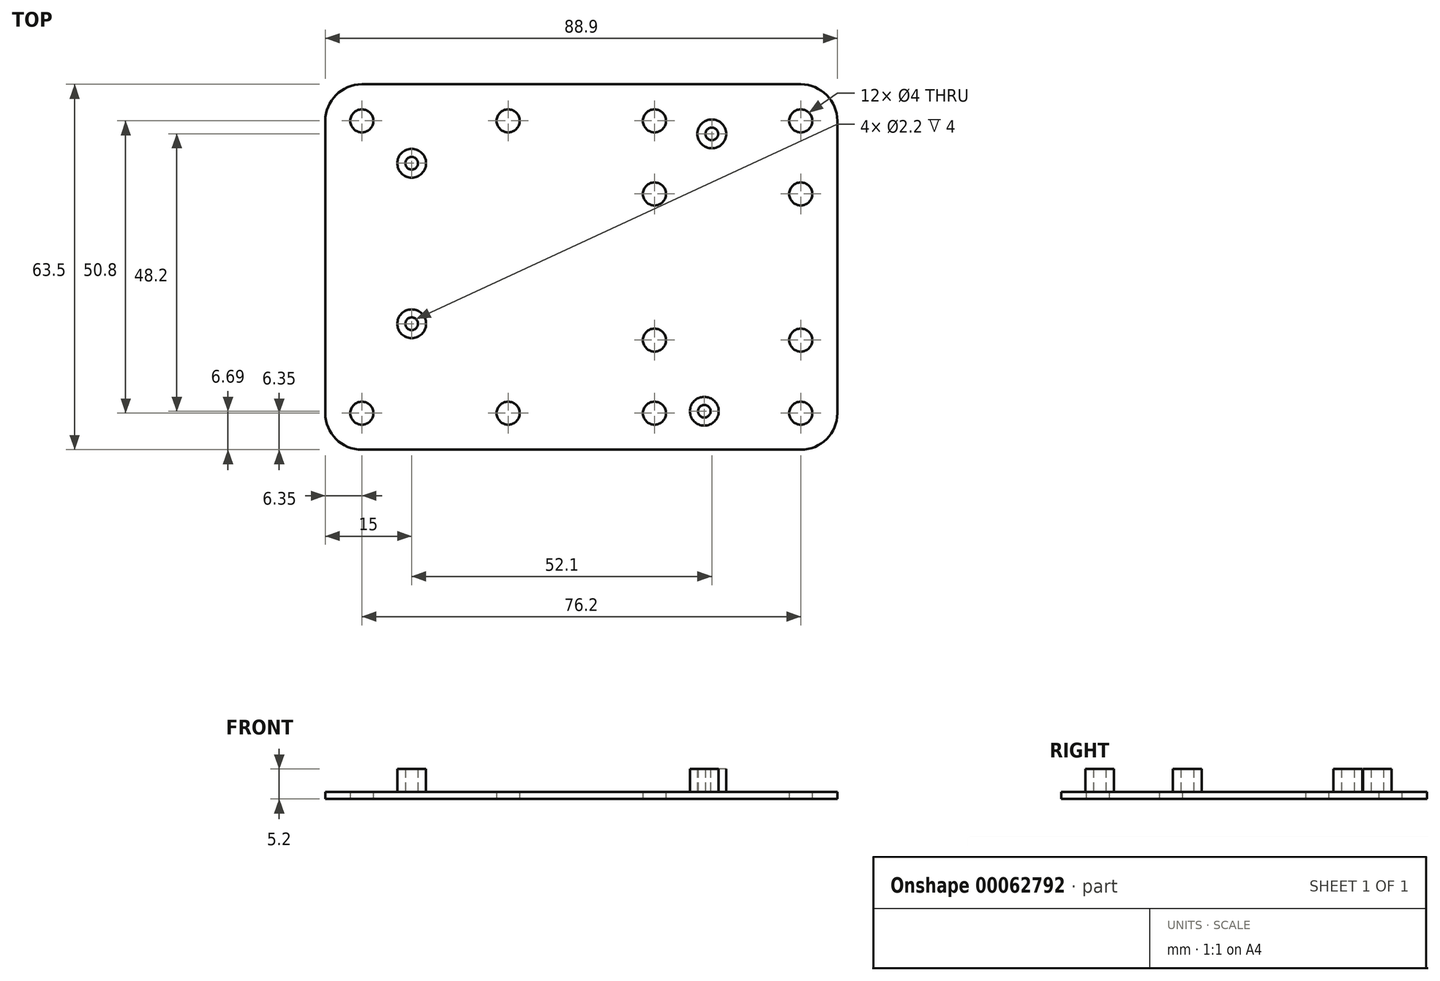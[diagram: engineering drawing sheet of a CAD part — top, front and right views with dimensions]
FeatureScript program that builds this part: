
annotation { "Feature Type Name" : "Feature", "Feature Type Description" : "" }
export const myFeature = defineFeature(function(context is Context, id is Id, definition is map)
    precondition{}
    {
        {
            var Q0;
            Q0=qCreatedBy(makeId("Top.planeOp"),FACE);
            var sketch = newSketch(context, id + "F0", { "sketchPlane" : qUnion([Q0])});
            skLineSegment(sketch, "E0.bottom", {"start": v(38.1, -31.75) * mm, "end": v(-38.1, -31.75) * mm});
            skLineSegment(sketch, "E0.top", {"start": v(38.1, 31.75) * mm, "end": v(-38.1, 31.75) * mm});
            skLineSegment(sketch, "E0.left", {"start": v(44.45, -25.4) * mm, "end": v(44.45, 25.4) * mm});
            skLineSegment(sketch, "E0.right", {"start": v(-44.45, -25.4) * mm, "end": v(-44.45, 25.4) * mm});
            skPoint(sketch, "E0.middle", {"position": v(0, 0) * mm});
            skPoint(sketch, "E1.visualSharp", {"position": v(-44.45, 31.75) * mm});
            skArc(sketch, "E1.filletArc", {"start": v(-38.1, 31.75) * mm, "mid": v(-42.6, 29.9) * mm, "end": v(-44.45, 25.4) * mm});
            skPoint(sketch, "E2.visualSharp", {"position": v(44.45, 31.75) * mm});
            skArc(sketch, "E2.filletArc", {"start": v(44.45, 25.4) * mm, "mid": v(42.6, 29.9) * mm, "end": v(38.1, 31.75) * mm});
            skPoint(sketch, "E3.visualSharp", {"position": v(44.45, -31.75) * mm});
            skArc(sketch, "E3.filletArc", {"start": v(38.1, -31.75) * mm, "mid": v(42.6, -29.9) * mm, "end": v(44.45, -25.4) * mm});
            skPoint(sketch, "E4.visualSharp", {"position": v(-44.45, -31.75) * mm});
            skArc(sketch, "E4.filletArc", {"start": v(-44.45, -25.4) * mm, "mid": v(-42.6, -29.9) * mm, "end": v(-38.1, -31.75) * mm});
            skCircle(sketch, "E5", {"center": v(-38.1, -25.4) * mm, "radius": 2 * mm});
            skCircle(sketch, "E6.0.1.0", {"center": v(-38.1, 25.4) * mm, "radius": 2 * mm});
            skCircle(sketch, "E6.1.0.0", {"center": v(-12.7, -25.4) * mm, "radius": 2 * mm});
            skCircle(sketch, "E6.1.1.0", {"center": v(-12.7, 25.4) * mm, "radius": 2 * mm});
            skCircle(sketch, "E6.2.0.0", {"center": v(12.7, -25.4) * mm, "radius": 2 * mm});
            skCircle(sketch, "E6.2.1.0", {"center": v(12.7, 25.4) * mm, "radius": 2 * mm});
            skLineSegment(sketch, "E6.direction1", {"start": v(-38.1, -25.4) * mm, "end": v(-12.7, -25.4) * mm, "construction": true});
            skLineSegment(sketch, "E6.direction2", {"start": v(-38.1, -25.4) * mm, "end": v(-38.1, 25.4) * mm, "construction": true});
            skCircle(sketch, "E7.0.3.0", {"center": v(38.1, -25.4) * mm, "radius": 2 * mm});
            skCircle(sketch, "E7.0.3.1", {"center": v(38.1, 25.4) * mm, "radius": 2 * mm});
            skCircle(sketch, "E8.0.1.0", {"center": v(38.1, -12.7) * mm, "radius": 2 * mm});
            skLineSegment(sketch, "E8.direction1", {"start": v(38.1, -25.4) * mm, "end": v(25.4, -25.4) * mm, "construction": true});
            skLineSegment(sketch, "E8.direction2", {"start": v(38.1, -25.4) * mm, "end": v(38.1, -12.7) * mm, "construction": true});
            skCircle(sketch, "E9.0.1.0", {"center": v(38.1, 12.7) * mm, "radius": 2 * mm});
            skCircle(sketch, "E9.1.0.0", {"center": v(12.7, -12.7) * mm, "radius": 2 * mm});
            skCircle(sketch, "E9.1.1.0", {"center": v(12.7, 12.7) * mm, "radius": 2 * mm});
            skLineSegment(sketch, "E9.direction1", {"start": v(38.1, -12.7) * mm, "end": v(12.7, -12.7) * mm, "construction": true});
            skLineSegment(sketch, "E9.direction2", {"start": v(38.1, -12.7) * mm, "end": v(38.1, 12.7) * mm, "construction": true});
            skSolve(sketch);
        }
        {
            var Q0;
            Q0=makeQuery(id+"F0.imprint","IMPRINT",FACE,{"disambiguationData":[TD([[makeQuery(id+"F0.imprint","IMPRINT",EDGE,{"derivedFrom":sQuery(id+"F0.wireOp",EDGE,"E0.bottom")}),-1.0]])]});
            extrude(context, id + "F1", {"entities" : qUnion([Q0]), "depth" : 1.2 * mm});
        }
        {
            var Q0;
            Q0=makeQuery(id+"F1.opExtrude","CAP_FACE",FACE,{"disambiguationData":[OSD([sQuery(id+"F0.wireOp",EDGE,"E0.bottom"),sQuery(id+"F0.wireOp",EDGE,"E0.top"),sQuery(id+"F0.wireOp",EDGE,"E0.left"),sQuery(id+"F0.wireOp",EDGE,"E0.right"),sQuery(id+"F0.wireOp",EDGE,"E1.filletArc"),sQuery(id+"F0.wireOp",EDGE,"E2.filletArc"),sQuery(id+"F0.wireOp",EDGE,"E3.filletArc"),sQuery(id+"F0.wireOp",EDGE,"E4.filletArc"),sQuery(id+"F0.wireOp",EDGE,"E5"),sQuery(id+"F0.wireOp",EDGE,"E6.0.1.0"),sQuery(id+"F0.wireOp",EDGE,"E6.1.0.0"),sQuery(id+"F0.wireOp",EDGE,"E6.1.1.0"),sQuery(id+"F0.wireOp",EDGE,"E6.2.0.0"),sQuery(id+"F0.wireOp",EDGE,"E6.2.1.0")])],"isStart":false});
            var sketch = newSketch(context, id + "F2", { "sketchPlane" : qUnion([Q0])});
            skPoint(sketch, "E10", {"position": v(-29.45, 18.04) * mm});
            skPoint(sketch, "E11", {"position": v(-29.45, -9.86) * mm});
            skPoint(sketch, "E12", {"position": v(22.65, 23.14) * mm});
            skPoint(sketch, "E13", {"position": v(21.35, -25.06) * mm});
            skCircle(sketch, "E14", {"center": v(-29.45, 18.04) * mm, "radius": 2.5 * mm});
            skCircle(sketch, "E15", {"center": v(-29.45, -9.86) * mm, "radius": 2.5 * mm});
            skCircle(sketch, "E16", {"center": v(22.65, 23.14) * mm, "radius": 2.5 * mm});
            skCircle(sketch, "E17", {"center": v(21.35, -25.06) * mm, "radius": 2.5 * mm});
            skCircle(sketch, "E18", {"center": v(-29.45, 18.04) * mm, "radius": 1.1 * mm});
            skCircle(sketch, "E19", {"center": v(-29.45, -9.86) * mm, "radius": 1.1 * mm});
            skCircle(sketch, "E20", {"center": v(22.65, 23.14) * mm, "radius": 1.1 * mm});
            skCircle(sketch, "E21", {"center": v(21.35, -25.06) * mm, "radius": 1.1 * mm});
            skSolve(sketch);
        }
        {
            var Q0;
            Q0=makeQuery(id+"F2.imprint","IMPRINT",FACE,{"disambiguationData":[TD([[makeQuery(id+"F2.imprint","IMPRINT",EDGE,{"derivedFrom":sQuery(id+"F2.wireOp",EDGE,"E14")}),1.0]])]});
            var Q1;
            Q1=makeQuery(id+"F2.imprint","IMPRINT",FACE,{"disambiguationData":[TD([[makeQuery(id+"F2.imprint","IMPRINT",EDGE,{"derivedFrom":sQuery(id+"F2.wireOp",EDGE,"E15")}),1.0]])]});
            var Q2;
            Q2=makeQuery(id+"F2.imprint","IMPRINT",FACE,{"disambiguationData":[TD([[makeQuery(id+"F2.imprint","IMPRINT",EDGE,{"derivedFrom":sQuery(id+"F2.wireOp",EDGE,"E17")}),1.0]])]});
            var Q3;
            Q3=makeQuery(id+"F2.imprint","IMPRINT",FACE,{"disambiguationData":[TD([[makeQuery(id+"F2.imprint","IMPRINT",EDGE,{"derivedFrom":sQuery(id+"F2.wireOp",EDGE,"E16")}),1.0]])]});
            extrude(context, id + "F3", {"entities" : qUnion([Q0, Q1, Q2, Q3]), "operationType" : NewBodyOperationType.ADD, "depth" : 4 * mm});
        }
    });
